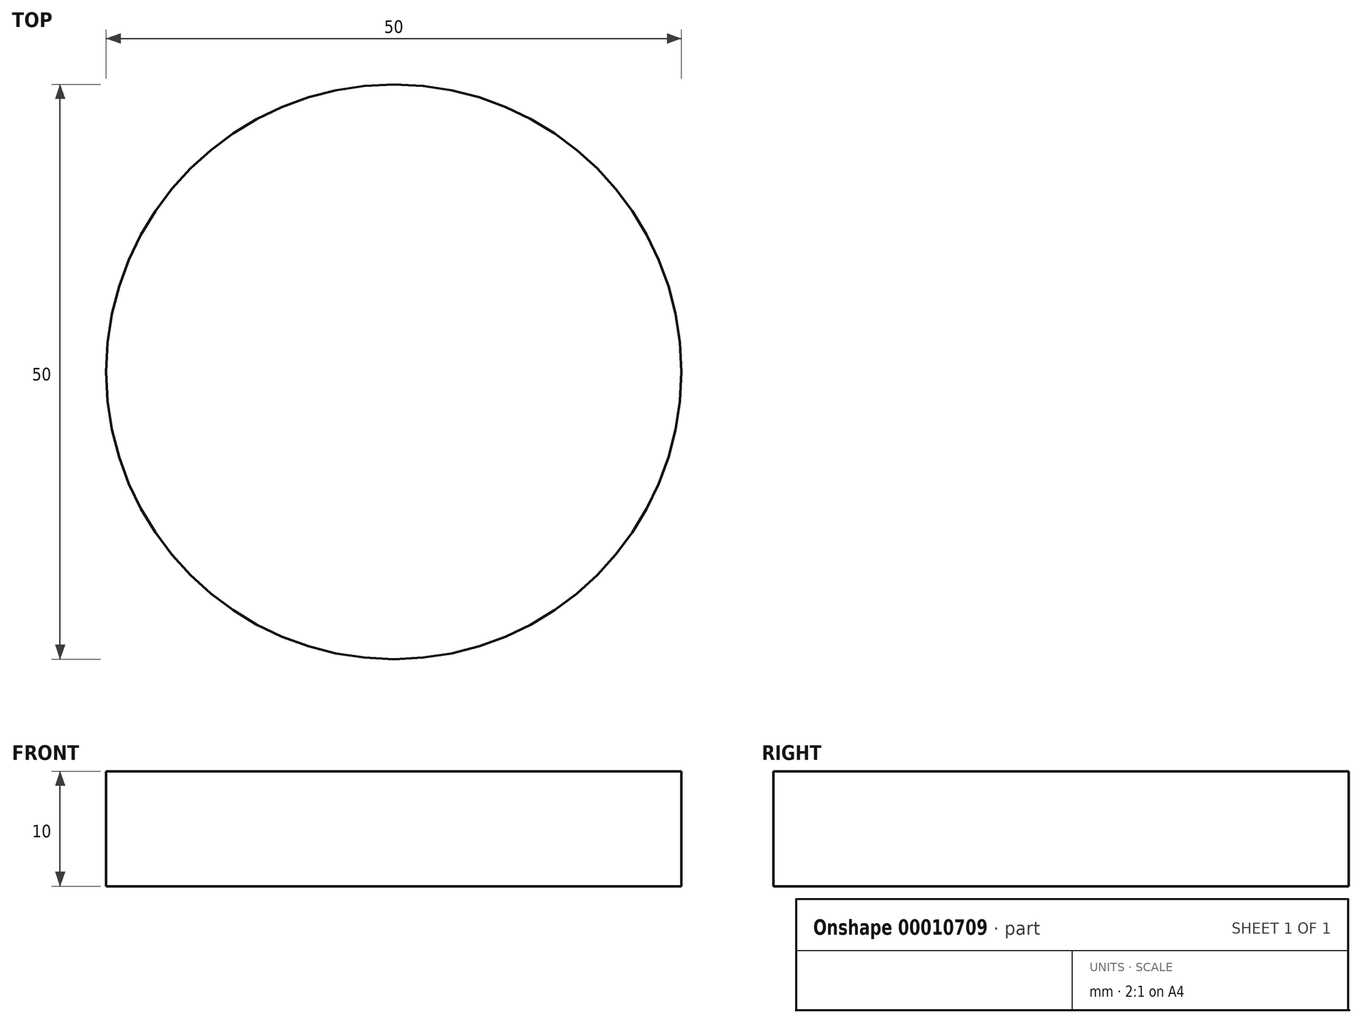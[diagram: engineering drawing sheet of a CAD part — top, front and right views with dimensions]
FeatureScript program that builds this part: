
annotation { "Feature Type Name" : "Feature", "Feature Type Description" : "" }
export const myFeature = defineFeature(function(context is Context, id is Id, definition is map)
    precondition{}
    {
        {
            var Q0;
            Q0=qCreatedBy(makeId("Top.planeOp"),FACE);
            var sketch = newSketch(context, id + "F0", { "sketchPlane" : qUnion([Q0])});
            skCircle(sketch, "E0", {"center": v(0, 0) * mm, "radius": 25 * mm});
            skCircle(sketch, "E1", {"center": v(0, 0) * mm, "radius": 25.55 * mm});
            skSolve(sketch);
        }
        {
            var Q0;
            Q0=makeQuery(id+"F0.imprint","IMPRINT",FACE,{"disambiguationData":[TD([[makeQuery(id+"F0.imprint","IMPRINT",EDGE,{"derivedFrom":sQuery(id+"F0.wireOp",EDGE,"E0")}),1.0]])]});
            extrude(context, id + "F1", {"entities" : qUnion([Q0]), "depth" : 10 * mm});
        }
    });
